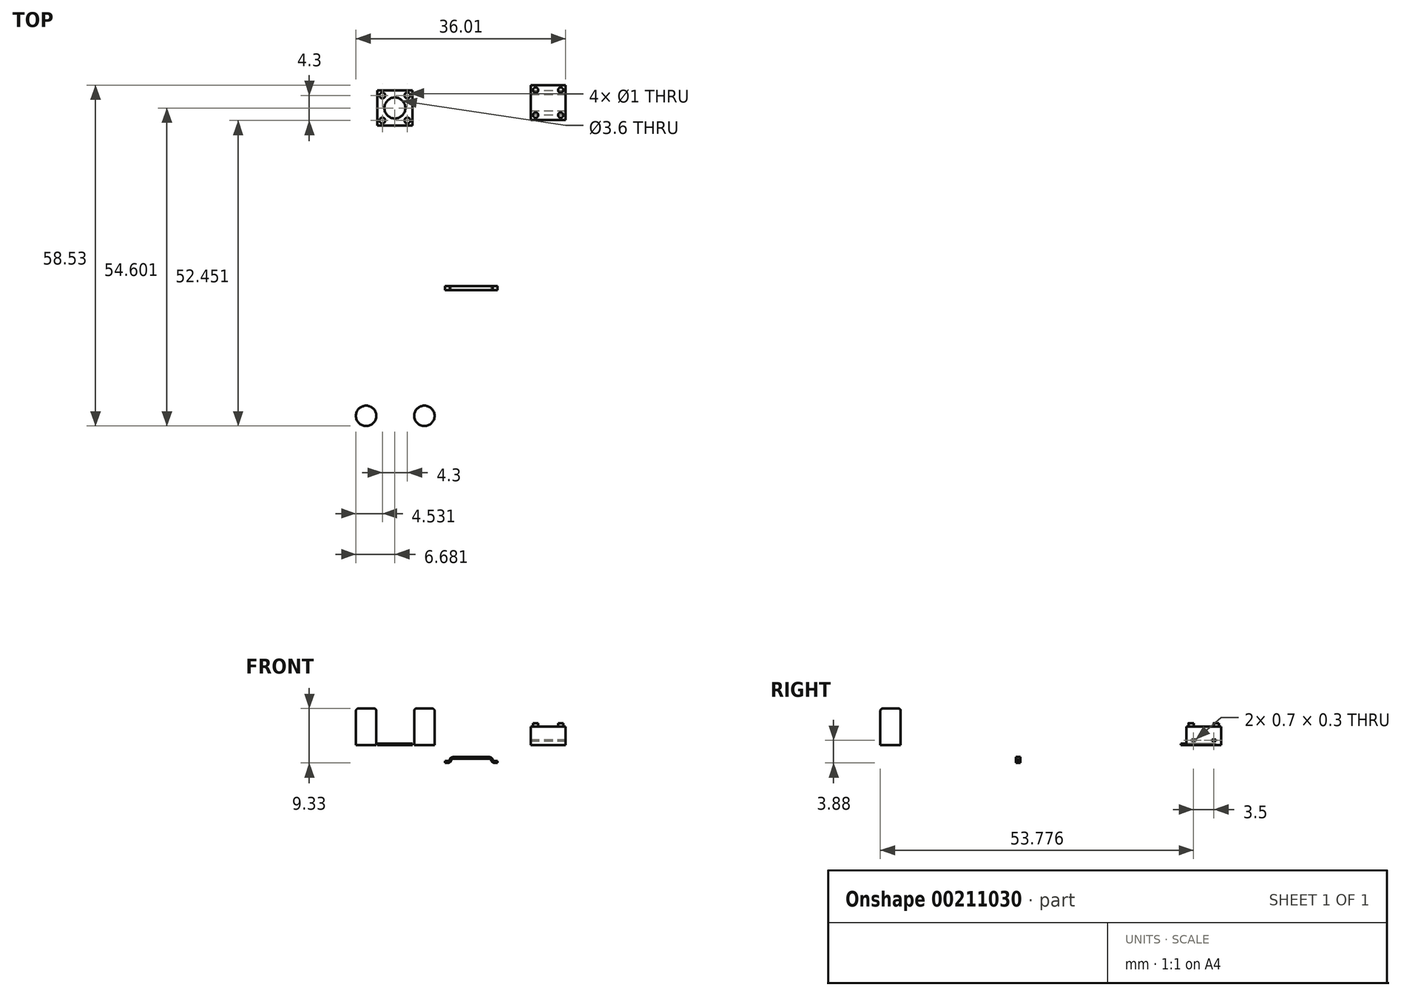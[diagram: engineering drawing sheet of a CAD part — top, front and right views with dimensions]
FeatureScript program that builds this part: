
annotation { "Feature Type Name" : "Feature", "Feature Type Description" : "" }
export const myFeature = defineFeature(function(context is Context, id is Id, definition is map)
    precondition{}
    {
        {
            var Q0;
            Q0=qCreatedBy(makeId("Front.planeOp"),FACE);
            var sketch = newSketch(context, id + "F0", { "sketchPlane" : qUnion([Q0])});
            skLineSegment(sketch, "E0", {"start": v(-4.5, -3.03) * mm, "end": v(-4, -3.03) * mm});
            skLineSegment(sketch, "E1", {"start": v(-3.42, -2.58) * mm, "end": v(-3.41, -2.54) * mm});
            skLineSegment(sketch, "E2", {"start": v(-3.12, -2.33) * mm, "end": v(0, -2.33) * mm});
            skPoint(sketch, "E3.visualSharp", {"position": v(-3.5, -3.03) * mm});
            skArc(sketch, "E3.filletArc", {"start": v(-4, -3.03) * mm, "mid": v(-3.62, -2.9) * mm, "end": v(-3.41, -2.54) * mm});
            skPoint(sketch, "E4.visualSharp", {"position": v(-3.38, -2.33) * mm});
            skArc(sketch, "E4.filletArc", {"start": v(-3.12, -2.33) * mm, "mid": v(-3.32, -2.4) * mm, "end": v(-3.42, -2.58) * mm});
            skLineSegment(sketch, "E5.0", {"start": v(-3.12, -2.03) * mm, "end": v(0, -2.03) * mm});
            skArc(sketch, "E5.1", {"start": v(-3.12, -2.03) * mm, "mid": v(-3.51, -2.17) * mm, "end": v(-3.72, -2.53) * mm});
            skLineSegment(sketch, "E5.2", {"start": v(-3.72, -2.53) * mm, "end": v(-3.7, -2.48) * mm});
            skLineSegment(sketch, "E5.3", {"start": v(-4.5, -2.73) * mm, "end": v(-4, -2.73) * mm});
            skLineSegment(sketch, "E6", {"start": v(-4.5, -2.73) * mm, "end": v(-4.5, -3.03) * mm});
            skPoint(sketch, "E7.visualSharp", {"position": v(-3.75, -2.73) * mm});
            skArc(sketch, "E7.filletArc", {"start": v(-4, -2.73) * mm, "mid": v(-3.81, -2.66) * mm, "end": v(-3.7, -2.48) * mm});
            skLineSegment(sketch, "E8.MirrorCS", {"start": v(4.5, -3.03) * mm, "end": v(4, -3.03) * mm});
            skLineSegment(sketch, "E9.MirrorCS", {"start": v(4.5, -2.73) * mm, "end": v(4, -2.73) * mm});
            skLineSegment(sketch, "E10.MirrorCS", {"start": v(4.5, -2.73) * mm, "end": v(4.5, -3.03) * mm});
            skArc(sketch, "E11.MirrorCS", {"start": v(3.12, -2.33) * mm, "mid": v(3.32, -2.4) * mm, "end": v(3.42, -2.58) * mm});
            skArc(sketch, "E12.MirrorCS", {"start": v(4, -2.73) * mm, "mid": v(3.81, -2.66) * mm, "end": v(3.7, -2.48) * mm});
            skArc(sketch, "E13.MirrorCS", {"start": v(3.12, -2.03) * mm, "mid": v(3.51, -2.17) * mm, "end": v(3.72, -2.53) * mm});
            skPoint(sketch, "E14.MirrorP", {"position": v(3.38, -2.33) * mm});
            skLineSegment(sketch, "E15.MirrorCS", {"start": v(3.12, -2.33) * mm, "end": v(0, -2.33) * mm});
            skArc(sketch, "E16.MirrorCS", {"start": v(4, -3.03) * mm, "mid": v(3.62, -2.9) * mm, "end": v(3.41, -2.54) * mm});
            skLineSegment(sketch, "E17.MirrorCS", {"start": v(3.42, -2.58) * mm, "end": v(3.41, -2.54) * mm});
            skLineSegment(sketch, "E18.MirrorCS", {"start": v(3.72, -2.53) * mm, "end": v(3.7, -2.48) * mm});
            skLineSegment(sketch, "E19.MirrorCS", {"start": v(3.12, -2.03) * mm, "end": v(0, -2.03) * mm});
            skPoint(sketch, "E20.MirrorP", {"position": v(3.5, -3.03) * mm});
            skPoint(sketch, "E21.MirrorP", {"position": v(3.75, -2.73) * mm});
            skSolve(sketch);
        }
        {
            var Q0;
            Q0 = qSketchRegion(id + "F0", true);
            extrude(context, id + "F1", {"entities" : qUnion([Q0]), "endBound" : BoundingType.SYMMETRIC, "depth" : .7 * mm});
        }
        {
            var Q0;
            Q0=qCreatedBy(makeId("Top.planeOp"),FACE);
            var sketch = newSketch(context, id + "F2", { "sketchPlane" : qUnion([Q0])});
            skLineSegment(sketch, "E22.bottom", {"start": v(10.22, 34.87) * mm, "end": v(16.22, 34.87) * mm});
            skLineSegment(sketch, "E22.top", {"start": v(10.22, 28.87) * mm, "end": v(16.22, 28.87) * mm});
            skLineSegment(sketch, "E22.left", {"start": v(10.22, 34.87) * mm, "end": v(10.22, 28.87) * mm});
            skLineSegment(sketch, "E22.right", {"start": v(16.22, 34.87) * mm, "end": v(16.22, 28.87) * mm});
            skSolve(sketch);
        }
        {
            var Q0;
            Q0 = qSketchRegion(id + "F2", true);
            extrude(context, id + "F3", {"entities" : qUnion([Q0]), "depth" : 3.2 * mm});
        }
        {
            var Q0;
            Q0=makeQuery(id+"F3.opExtrude","CAP_FACE",FACE,{"disambiguationData":[OSD([sQuery(id+"F2.wireOp",EDGE,"E22.bottom"),sQuery(id+"F2.wireOp",EDGE,"E22.top"),sQuery(id+"F2.wireOp",EDGE,"E22.left"),sQuery(id+"F2.wireOp",EDGE,"E22.right")])],"isStart":false});
            var sketch = newSketch(context, id + "F4", { "sketchPlane" : qUnion([Q0])});
            skCircle(sketch, "E23", {"center": v(11.07, 34.02) * mm, "radius": 0.45 * mm});
            skCircle(sketch, "E24", {"center": v(11.07, 29.72) * mm, "radius": 0.45 * mm});
            skCircle(sketch, "E25", {"center": v(15.37, 34.02) * mm, "radius": 0.45 * mm});
            skCircle(sketch, "E26", {"center": v(15.37, 29.72) * mm, "radius": 0.45 * mm});
            skSolve(sketch);
        }
        {
            var Q0;
            Q0 = qSketchRegion(id + "F4", true);
            extrude(context, id + "F5", {"entities" : qUnion([Q0]), "operationType" : NewBodyOperationType.ADD, "depth" : .6 * mm});
        }
        {
            var Q0;
            Q0=makeQuery(id+"F3.opExtrude","SWEPT_FACE",FACE,{"disambiguationData":[OSD([sQuery(id+"F2.wireOp",EDGE,"E22.right")])]});
            var sketch = newSketch(context, id + "F6", { "sketchPlane" : qUnion([Q0])});
            skLineSegment(sketch, "E27.bottom", {"start": v(29.77, 1) * mm, "end": v(30.47, 1) * mm});
            skLineSegment(sketch, "E27.top", {"start": v(29.77, 0.7) * mm, "end": v(30.47, 0.7) * mm});
            skLineSegment(sketch, "E27.left", {"start": v(29.77, 1) * mm, "end": v(29.77, 0.7) * mm});
            skLineSegment(sketch, "E27.right", {"start": v(30.47, 1) * mm, "end": v(30.47, 0.7) * mm});
            skLineSegment(sketch, "E28.bottom", {"start": v(33.27, 1) * mm, "end": v(33.97, 1) * mm});
            skLineSegment(sketch, "E28.top", {"start": v(33.27, 0.7) * mm, "end": v(33.97, 0.7) * mm});
            skLineSegment(sketch, "E28.left", {"start": v(33.27, 1) * mm, "end": v(33.27, 0.7) * mm});
            skLineSegment(sketch, "E28.right", {"start": v(33.97, 1) * mm, "end": v(33.97, 0.7) * mm});
            skPoint(sketch, "E29", {"position": v(30.12, 0.7) * mm});
            skPoint(sketch, "E30", {"position": v(33.62, 0.7) * mm});
            skSolve(sketch);
        }
        {
            var Q0;
            Q0=makeQuery(id+"F6.imprint","IMPRINT",FACE,{"disambiguationData":[TD([[makeQuery(id+"F6.imprint","IMPRINT",EDGE,{"derivedFrom":sQuery(id+"F6.wireOp",EDGE,"E27.bottom")}),-1.0]])]});
            var Q1;
            Q1=makeQuery(id+"F6.imprint","IMPRINT",FACE,{"disambiguationData":[TD([[makeQuery(id+"F6.imprint","IMPRINT",EDGE,{"derivedFrom":sQuery(id+"F6.wireOp",EDGE,"E28.bottom")}),-1.0]])]});
            extrude(context, id + "F7", {"entities" : qUnion([Q0, Q1]), "operationType" : NewBodyOperationType.REMOVE, "endBound" : BoundingType.THROUGH_ALL, "oppositeDirection" : true, "depth" : 25 * mm});
        }
        {
            var Q0;
            Q0=qCreatedBy(makeId("Top.planeOp"),FACE);
            var sketch = newSketch(context, id + "F8", { "sketchPlane" : qUnion([Q0])});
            skLineSegment(sketch, "E31.bottom", {"start": v(-16.1, 33.94) * mm, "end": v(-10.1, 33.94) * mm});
            skLineSegment(sketch, "E31.top", {"start": v(-16.1, 27.94) * mm, "end": v(-10.1, 27.94) * mm});
            skLineSegment(sketch, "E31.left", {"start": v(-16.1, 33.94) * mm, "end": v(-16.1, 27.94) * mm});
            skLineSegment(sketch, "E31.right", {"start": v(-10.1, 33.94) * mm, "end": v(-10.1, 27.94) * mm});
            skSolve(sketch);
        }
        {
            var Q0;
            Q0 = qSketchRegion(id + "F8", true);
            extrude(context, id + "F9", {"entities" : qUnion([Q0]), "depth" : .3 * mm});
        }
        {
            var Q0;
            Q0=makeQuery(id+"F9.opExtrude","CAP_FACE",FACE,{"disambiguationData":[OSD([sQuery(id+"F8.wireOp",EDGE,"E31.bottom"),sQuery(id+"F8.wireOp",EDGE,"E31.top"),sQuery(id+"F8.wireOp",EDGE,"E31.left"),sQuery(id+"F8.wireOp",EDGE,"E31.right")])],"isStart":false});
            var sketch = newSketch(context, id + "F10", { "sketchPlane" : qUnion([Q0])});
            skCircle(sketch, "E32", {"center": v(-15.26, 28.8) * mm, "radius": 0.5 * mm});
            skCircle(sketch, "E33", {"center": v(-15.26, 33.1) * mm, "radius": 0.5 * mm});
            skCircle(sketch, "E34", {"center": v(-10.96, 33.1) * mm, "radius": 0.5 * mm});
            skCircle(sketch, "E35", {"center": v(-10.96, 28.8) * mm, "radius": 0.5 * mm});
            skCircle(sketch, "E36", {"center": v(-13.1, 30.94) * mm, "radius": 1.8 * mm});
            skSolve(sketch);
        }
        {
            var Q0;
            Q0 = qSketchRegion(id + "F10", true);
            extrude(context, id + "F11", {"entities" : qUnion([Q0]), "operationType" : NewBodyOperationType.REMOVE, "endBound" : BoundingType.THROUGH_ALL, "oppositeDirection" : true, "depth" : 25 * mm});
        }
        {
            var Q0;
            Q0=qCreatedBy(makeId("Top.planeOp"),FACE);
            var sketch = newSketch(context, id + "F12", { "sketchPlane" : qUnion([Q0])});
            skCircle(sketch, "E37", {"center": v(-18.04, -21.91) * mm, "radius": 1.75 * mm});
            skSolve(sketch);
        }
        {
            var Q0;
            Q0 = qSketchRegion(id + "F12", true);
            extrude(context, id + "F13", {"entities" : qUnion([Q0]), "depth" : 6.3 * mm});
        }
        {
            var Q0;
            Q0=makeQuery(id+"F13.opExtrude","CAP_EDGE",EDGE,{"disambiguationData":[OSD([sQuery(id+"F12.wireOp",EDGE,"E37")])],"isStart":false});
            fillet(context, id + "F14", {"entities" : qUnion([Q0]), "radius" : .4 * mm, "tangentPropagation" : true, "allowEdgeOverflow" : false});
        }
        {
            var Q0;
            Q0=makeQuery(id+"F13.opExtrude","SWEPT_BODY",BODY,{"disambiguationData":[OSD([sQuery(id+"F12.wireOp",EDGE,"E37")])]});
            transform(context, id + "F15", {"entities" : qUnion([Q0]), "transformType" : TransformType.TRANSLATION_3D, "dx" : 10 * mm, "dy" : 0 * mm, "dz" : 0 * mm, "makeCopy" : true});
        }
    });
